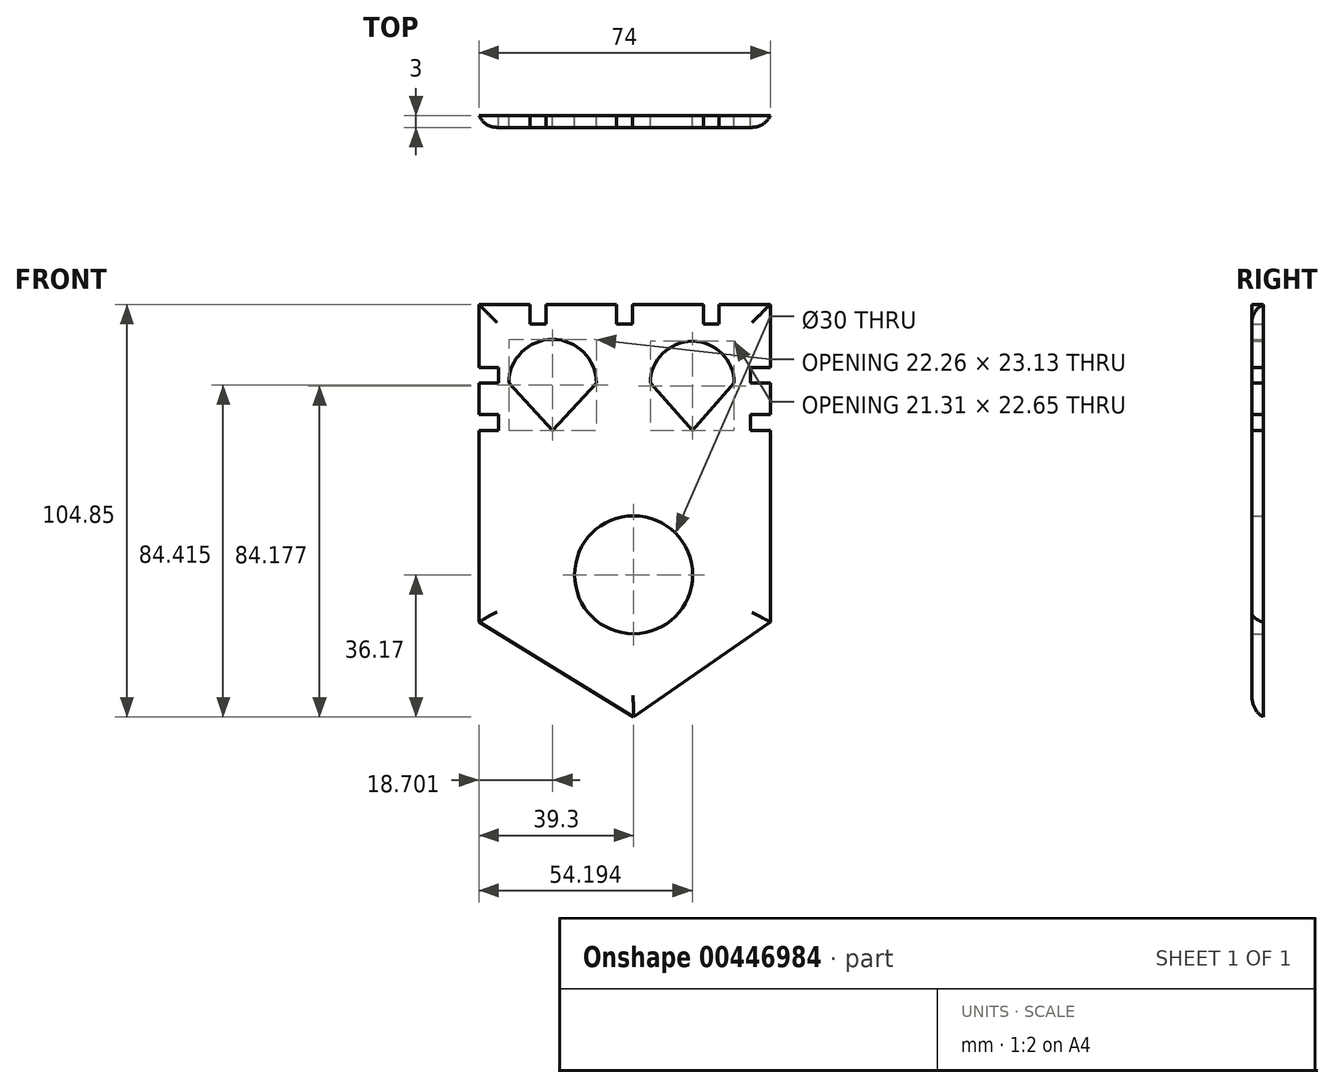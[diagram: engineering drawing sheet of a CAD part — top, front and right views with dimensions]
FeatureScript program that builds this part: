
annotation { "Feature Type Name" : "Feature", "Feature Type Description" : "" }
export const myFeature = defineFeature(function(context is Context, id is Id, definition is map)
    precondition{}
    {
        {
            var Q0;
            Q0=qCreatedBy(makeId("Front.planeOp"),FACE);
            var sketch = newSketch(context, id + "F0", { "sketchPlane" : qUnion([Q0])});
            skLineSegment(sketch, "E0.top", {"start": v(-39.3, -40.66) * mm, "end": v(34.7, -40.66) * mm});
            skLineSegment(sketch, "E0.left", {"start": v(-39.3, 0) * mm, "end": v(-39.3, -40.66) * mm});
            skLineSegment(sketch, "E0.right", {"start": v(34.7, 0) * mm, "end": v(34.7, -40.66) * mm});
            skLineSegment(sketch, "E1.top", {"start": v(-39.3, 40) * mm, "end": v(-26.3, 40) * mm});
            skLineSegment(sketch, "E1.left", {"start": v(-39.3, 0) * mm, "end": v(-39.3, 8) * mm});
            skLineSegment(sketch, "E1.right", {"start": v(34.7, 0) * mm, "end": v(34.7, 8) * mm});
            skLineSegment(sketch, "E2", {"start": v(-39.3, -40.66) * mm, "end": v(0, -64.85) * mm});
            skLineSegment(sketch, "E3", {"start": v(34.7, -40.66) * mm, "end": v(0, -64.85) * mm});
            skPoint(sketch, "E4.top.end.orphan", {"position": v(-4.3, 35) * mm});
            skLineSegment(sketch, "E5.top", {"start": v(-0.3, 35) * mm, "end": v(-4.3, 35) * mm});
            skLineSegment(sketch, "E5.left", {"start": v(-0.3, 40) * mm, "end": v(-0.3, 35) * mm});
            skLineSegment(sketch, "E5.right", {"start": v(-4.3, 40) * mm, "end": v(-4.3, 35) * mm});
            skLineSegment(sketch, "E6.top", {"start": v(17.7, 35) * mm, "end": v(21.7, 35) * mm});
            skLineSegment(sketch, "E6.left", {"start": v(17.7, 40) * mm, "end": v(17.7, 35) * mm});
            skLineSegment(sketch, "E6.right", {"start": v(21.7, 40) * mm, "end": v(21.7, 35) * mm});
            skLineSegment(sketch, "E7.trimOffspring", {"start": v(21.7, 40) * mm, "end": v(34.7, 40) * mm});
            skLineSegment(sketch, "E8.trimOffspring", {"start": v(-0.3, 40) * mm, "end": v(17.7, 40) * mm});
            skPoint(sketch, "E4.bottom.start.orphan", {"position": v(0, 40) * mm});
            skPoint(sketch, "E9.top.end.orphan", {"position": v(-24.8, 35) * mm});
            skLineSegment(sketch, "E10.top", {"start": v(-26.3, 35) * mm, "end": v(-22.3, 35) * mm});
            skLineSegment(sketch, "E10.left", {"start": v(-26.3, 40) * mm, "end": v(-26.3, 35) * mm});
            skLineSegment(sketch, "E10.right", {"start": v(-22.3, 40) * mm, "end": v(-22.3, 35) * mm});
            skPoint(sketch, "E11.oppositeSnap0", {"position": v(-39.3, 20) * mm});
            skLineSegment(sketch, "E11.bottom", {"start": v(-39.3, 24) * mm, "end": v(-34.3, 24) * mm});
            skLineSegment(sketch, "E11.top", {"start": v(-39.3, 20) * mm, "end": v(-34.3, 20) * mm});
            skLineSegment(sketch, "E11.right", {"start": v(-34.3, 24) * mm, "end": v(-34.3, 20) * mm});
            skLineSegment(sketch, "E12.trimOffspring", {"start": v(-39.3, 24) * mm, "end": v(-39.3, 40) * mm});
            skLineSegment(sketch, "E13", {"start": v(21.7, 35) * mm, "end": v(17.7, 35) * mm});
            skPoint(sketch, "E14.end.orphan", {"position": v(-29.9, 35) * mm});
            skPoint(sketch, "E14.start.orphan", {"position": v(-39.3, 32) * mm});
            skLineSegment(sketch, "E15.trimOffspring", {"start": v(-4.3, 35) * mm, "end": v(-0.3, 35) * mm});
            skLineSegment(sketch, "E16.trimOffspring", {"start": v(-22.3, 35) * mm, "end": v(-26.3, 35) * mm});
            skPoint(sketch, "E17.orphan", {"position": v(-22.3, 42.56) * mm});
            skLineSegment(sketch, "E18.trimOffspring", {"start": v(-22.3, 40) * mm, "end": v(-4.3, 40) * mm});
            skPoint(sketch, "E19.endSnap0", {"position": v(34.7, 20) * mm});
            skPoint(sketch, "E19.end.orphan", {"position": v(29.7, 20) * mm});
            skLineSegment(sketch, "E20.bottom", {"start": v(34.7, 24) * mm, "end": v(34.7, 24) * mm});
            skLineSegment(sketch, "E20.top", {"start": v(34.7, 20) * mm, "end": v(34.7, 20) * mm});
            skLineSegment(sketch, "E21.bottom", {"start": v(34.7, 24) * mm, "end": v(29.7, 24) * mm});
            skLineSegment(sketch, "E21.top", {"start": v(34.7, 20) * mm, "end": v(29.7, 20) * mm});
            skLineSegment(sketch, "E21.right", {"start": v(29.7, 24) * mm, "end": v(29.7, 20) * mm});
            skLineSegment(sketch, "E22.trimOffspring", {"start": v(29.7, 24) * mm, "end": v(34.7, 24) * mm});
            skLineSegment(sketch, "E23.bottom", {"start": v(-39.3, 12) * mm, "end": v(-34.3, 12) * mm});
            skLineSegment(sketch, "E23.top", {"start": v(-39.3, 8) * mm, "end": v(-34.3, 8) * mm});
            skLineSegment(sketch, "E23.right", {"start": v(-34.3, 12) * mm, "end": v(-34.3, 8) * mm});
            skLineSegment(sketch, "E24.bottom", {"start": v(34.7, 12) * mm, "end": v(29.7, 12) * mm});
            skLineSegment(sketch, "E24.top", {"start": v(34.7, 8) * mm, "end": v(29.7, 8) * mm});
            skLineSegment(sketch, "E24.right", {"start": v(29.7, 12) * mm, "end": v(29.7, 8) * mm});
            skLineSegment(sketch, "E25.trimOffspring", {"start": v(-39.3, 12) * mm, "end": v(-39.3, 20) * mm});
            skLineSegment(sketch, "E26.trimOffspring", {"start": v(34.7, 12) * mm, "end": v(34.7, 20) * mm});
            skLineSegment(sketch, "E27.trimOffspring", {"start": v(34.7, 24) * mm, "end": v(34.7, 40) * mm});
            skCircle(sketch, "E28", {"center": v(0, -28.68) * mm, "radius": 15 * mm});
            skArc(sketch, "E29", {"start": v(-9.47, 20) * mm, "mid": v(-20.6, 31.13) * mm, "end": v(-31.73, 20) * mm});
            skArc(sketch, "E30", {"start": v(25.55, 20) * mm, "mid": v(14.9, 30.65) * mm, "end": v(4.24, 20) * mm});
            skLineSegment(sketch, "E31", {"start": v(-31.73, 20) * mm, "end": v(-20.6, 8) * mm});
            skLineSegment(sketch, "E32", {"start": v(-20.6, 8) * mm, "end": v(-9.47, 20) * mm});
            skLineSegment(sketch, "E33", {"start": v(4.24, 20) * mm, "end": v(14.9, 8) * mm});
            skLineSegment(sketch, "E34", {"start": v(14.9, 8) * mm, "end": v(25.55, 20) * mm});
            skSolve(sketch);
        }
        {
            var Q0;
            Q0 = qSketchRegion(id + "F0", true);
            extrude(context, id + "F1", {"entities" : qUnion([Q0]), "depth" : 3 * mm});
        }
        {
            var Q0;
            Q0=makeQuery(id+"F1.opExtrude","CAP_EDGE",EDGE,{"disambiguationData":[OSD([sQuery(id+"F0.wireOp",EDGE,"E2")])],"isStart":false});
            var Q1;
            Q1=makeQuery(id+"F1.opExtrude","CAP_EDGE",EDGE,{"disambiguationData":[OSD([sQuery(id+"F0.wireOp",EDGE,"E3")])],"isStart":false});
            var Q2;
            Q2=makeQuery(id+"F1.opExtrude","CAP_EDGE",EDGE,{"disambiguationData":[OSD([sQuery(id+"F0.wireOp",EDGE,"E0.left"),sQuery(id+"F0.wireOp",EDGE,"E1.left")])],"isStart":false});
            var Q3;
            Q3=makeQuery(id+"F1.opExtrude","CAP_EDGE",EDGE,{"disambiguationData":[OSD([sQuery(id+"F0.wireOp",EDGE,"E25.trimOffspring")])],"isStart":false});
            var Q4;
            Q4=makeQuery(id+"F1.opExtrude","CAP_EDGE",EDGE,{"disambiguationData":[OSD([sQuery(id+"F0.wireOp",EDGE,"E12.trimOffspring")])],"isStart":false});
            var Q5;
            Q5=makeQuery(id+"F1.opExtrude","CAP_EDGE",EDGE,{"disambiguationData":[OSD([sQuery(id+"F0.wireOp",EDGE,"E1.top")])],"isStart":false});
            var Q6;
            Q6=makeQuery(id+"F1.opExtrude","CAP_EDGE",EDGE,{"disambiguationData":[OSD([sQuery(id+"F0.wireOp",EDGE,"E18.trimOffspring")])],"isStart":false});
            var Q7;
            Q7=makeQuery(id+"F1.opExtrude","CAP_EDGE",EDGE,{"disambiguationData":[OSD([sQuery(id+"F0.wireOp",EDGE,"E8.trimOffspring")])],"isStart":false});
            var Q8;
            Q8=makeQuery(id+"F1.opExtrude","CAP_EDGE",EDGE,{"disambiguationData":[OSD([sQuery(id+"F0.wireOp",EDGE,"E7.trimOffspring")])],"isStart":false});
            var Q9;
            Q9=makeQuery(id+"F1.opExtrude","CAP_EDGE",EDGE,{"disambiguationData":[OSD([sQuery(id+"F0.wireOp",EDGE,"E27.trimOffspring")])],"isStart":false});
            var Q10;
            Q10=makeQuery(id+"F1.opExtrude","CAP_EDGE",EDGE,{"disambiguationData":[OSD([sQuery(id+"F0.wireOp",EDGE,"E26.trimOffspring")])],"isStart":false});
            var Q11;
            Q11=makeQuery(id+"F1.opExtrude","CAP_EDGE",EDGE,{"disambiguationData":[OSD([sQuery(id+"F0.wireOp",EDGE,"E0.right"),sQuery(id+"F0.wireOp",EDGE,"E1.right")])],"isStart":false});
            fillet(context, id + "F2", {"entities" : qUnion([Q0, Q1, Q2, Q3, Q4, Q5, Q6, Q7, Q8, Q9, Q10, Q11]), "radius" : 5 * mm, "tangentPropagation" : true, "allowEdgeOverflow" : false});
        }
    });
